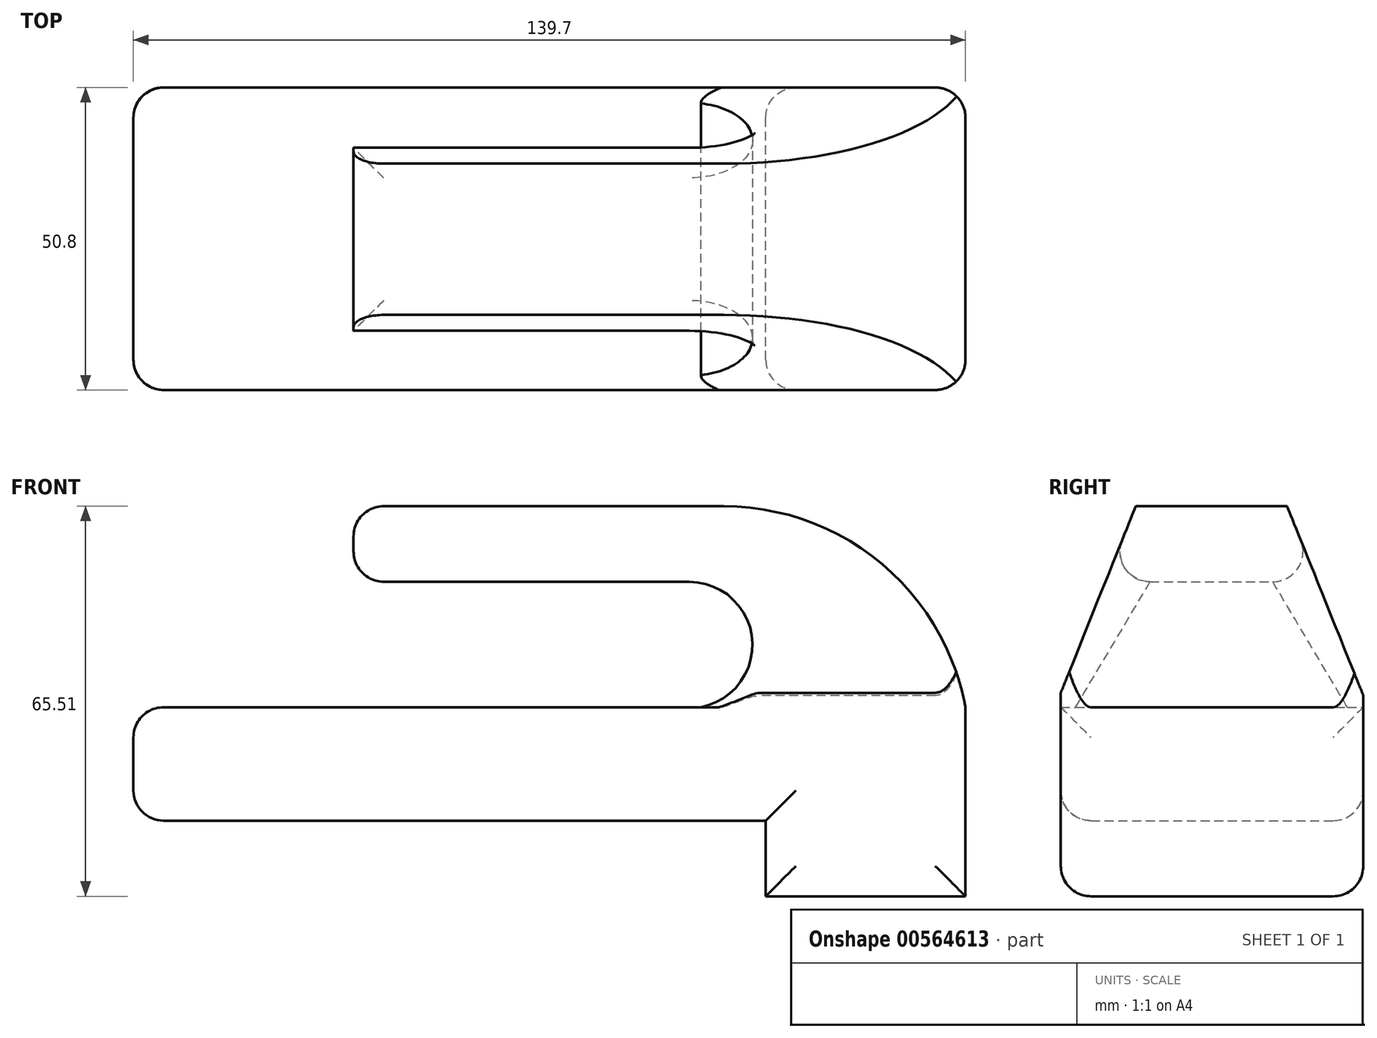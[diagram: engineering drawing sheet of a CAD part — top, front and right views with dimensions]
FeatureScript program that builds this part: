
annotation { "Feature Type Name" : "Feature", "Feature Type Description" : "" }
export const myFeature = defineFeature(function(context is Context, id is Id, definition is map)
    precondition{}
    {
        {
            var Q0;
            Q0=qCreatedBy(makeId("Front.planeOp"),FACE);
            var sketch = newSketch(context, id + "F0", { "sketchPlane" : qUnion([Q0])});
            skLineSegment(sketch, "E0.top", {"start": v(-62.26, -21) * mm, "end": v(77.44, -21) * mm});
            skLineSegment(sketch, "E0.left", {"start": v(-62.26, -1.96) * mm, "end": v(-62.26, -21) * mm});
            skLineSegment(sketch, "E0.right", {"start": v(77.44, -1.96) * mm, "end": v(77.44, -21) * mm});
            skLineSegment(sketch, "E1", {"start": v(-25.3, 31.81) * mm, "end": v(36.87, 31.81) * mm});
            skArc(sketch, "E2", {"start": v(77.44, -1.96) * mm, "mid": v(63.26, 22.26) * mm, "end": v(36.87, 31.81) * mm});
            skLineSegment(sketch, "E3", {"start": v(-25.3, 31.81) * mm, "end": v(-25.3, 19.11) * mm});
            skLineSegment(sketch, "E4", {"start": v(-25.3, 19.11) * mm, "end": v(31.09, 19.11) * mm});
            skArc(sketch, "E5", {"start": v(33.02, -1.96) * mm, "mid": v(41.67, 9.46) * mm, "end": v(31.09, 19.11) * mm});
            skLineSegment(sketch, "E6", {"start": v(-62.26, -1.96) * mm, "end": v(33.02, -1.96) * mm});
            skLineSegment(sketch, "E7.bottom", {"start": v(77.44, -21) * mm, "end": v(43.9, -21) * mm});
            skLineSegment(sketch, "E7.top", {"start": v(77.44, -33.7) * mm, "end": v(43.9, -33.7) * mm});
            skLineSegment(sketch, "E7.left", {"start": v(77.44, -21) * mm, "end": v(77.44, -33.7) * mm});
            skLineSegment(sketch, "E7.right", {"start": v(43.9, -21) * mm, "end": v(43.9, -33.7) * mm});
            skSolve(sketch);
        }
        {
            var Q0;
            Q0=qSketchRegion(id+"F0",true);
            var Q1;
            Q1 = qSketchRegion(id + "F2", true);
            extrude(context, id + "F1", {"entities" : qUnion([Q0, Q1]), "depth" : 50.8 * mm, "offsetDistance" : 25.4 * mm});
        }
        {
            var Q0;
            Q0=qCreatedBy(makeId("Right.planeOp"),FACE);
            var sketch = newSketch(context, id + "F2", { "sketchPlane" : qUnion([Q0])});
            skLineSegment(sketch, "E8", {"start": v(-12.8, 31.81) * mm, "end": v(0, 0) * mm});
            skLineSegment(sketch, "E9", {"start": v(0, 31.81) * mm, "end": v(-12.8, 31.81) * mm});
            skLineSegment(sketch, "E10", {"start": v(-38.2, 31.81) * mm, "end": v(-50.99, 0) * mm});
            skLineSegment(sketch, "E11", {"start": v(-50.99, 31.81) * mm, "end": v(-38.2, 31.81) * mm});
            skLineSegment(sketch, "E12", {"start": v(-50.99, 0) * mm, "end": v(-50.99, 31.81) * mm});
            skLineSegment(sketch, "E13", {"start": v(0, 31.81) * mm, "end": v(0, 0) * mm});
            skSolve(sketch);
        }
        {
            var Q0;
            Q0=qSketchRegion(id+"F2",true);
            extrude(context, id + "F3", {"entities" : qUnion([Q0]), "operationType" : NewBodyOperationType.REMOVE, "oppositeDirection" : true, "depth" : -152.4 * mm, "offsetDistance" : 25.4 * mm});
        }
        {
            var Q0;
            Q0=qSketchRegion(id+"F2",true);
            extrude(context, id + "F4", {"entities" : qUnion([Q0]), "operationType" : NewBodyOperationType.REMOVE, "oppositeDirection" : true, "depth" : 50.8 * mm, "offsetDistance" : 25.4 * mm});
        }
        {
            var Q0;
            {var subQ0=sQuery(id+"F2.wireOp",EDGE,"E9");var subQ1=sQuery(id+"F2.wireOp",EDGE,"E8");Q0=makeQuery(id+"F4.boolean.opBoolean","MERGE",EDGE,{"derivedFrom":[makeQuery(id+"F3.boolean.opBoolean","COPY",EDGE,{"derivedFrom":makeQuery(id+"F3.opExtrude","SWEPT_EDGE",EDGE,{"disambiguationData":[OSD([subQ1,subQ0])]})}),makeQuery(id+"F4.opExtrude","SWEPT_EDGE",EDGE,{"disambiguationData":[OSD([subQ1,subQ0])]})]});}
            var Q1;
            {var subQ0=sQuery(id+"F2.wireOp",EDGE,"E11");var subQ1=sQuery(id+"F2.wireOp",EDGE,"E10");Q1=makeQuery(id+"F4.boolean.opBoolean","MERGE",EDGE,{"derivedFrom":[makeQuery(id+"F3.boolean.opBoolean","COPY",EDGE,{"derivedFrom":makeQuery(id+"F3.opExtrude","SWEPT_EDGE",EDGE,{"disambiguationData":[OSD([subQ1,subQ0])]})}),makeQuery(id+"F4.opExtrude","SWEPT_EDGE",EDGE,{"disambiguationData":[OSD([subQ1,subQ0])]})]});}
            var Q2;
            Q2=makeQuery(id+"F4.boolean.opBoolean","INTERSECT",EDGE,{"derivedFrom":[makeQuery(id+"F1.opExtrude","SWEPT_FACE",FACE,{"disambiguationData":[OSD([sQuery(id+"F0.wireOp",EDGE,"E4")])]}),makeQuery(id+"F4.opExtrude","SWEPT_FACE",FACE,{"disambiguationData":[OSD([sQuery(id+"F2.wireOp",EDGE,"E8")])]})]});
            var Q3;
            Q3=makeQuery(id+"F1.opExtrude","SWEPT_EDGE",EDGE,{"disambiguationData":[OSD([sQuery(id+"F0.wireOp",EDGE,"E3"),sQuery(id+"F0.wireOp",EDGE,"E4")])]});
            var Q4;
            Q4=makeQuery(id+"F4.boolean.opBoolean","INTERSECT",EDGE,{"derivedFrom":[makeQuery(id+"F1.opExtrude","SWEPT_FACE",FACE,{"disambiguationData":[OSD([sQuery(id+"F0.wireOp",EDGE,"E4")])]}),makeQuery(id+"F4.opExtrude","SWEPT_FACE",FACE,{"disambiguationData":[OSD([sQuery(id+"F2.wireOp",EDGE,"E10")])]})]});
            fillet(context, id + "F5", {"entities" : qUnion([Q0, Q1, Q2, Q3, Q4]), "radius" : 5.08 * mm, "tangentPropagation" : true, "allowEdgeOverflow" : false});
        }
        {
            var Q0;
            Q0=makeQuery(id+"F1.opExtrude","SWEPT_EDGE",EDGE,{"disambiguationData":[OSD([sQuery(id+"F0.wireOp",EDGE,"E0.left"),sQuery(id+"F0.wireOp",EDGE,"E6")])]});
            var Q1;
            Q1=makeQuery(id+"F1.opExtrude","SWEPT_EDGE",EDGE,{"disambiguationData":[OSD([sQuery(id+"F0.wireOp",EDGE,"E0.top"),sQuery(id+"F0.wireOp",EDGE,"E0.left")])]});
            var Q2;
            Q2=makeQuery(id+"F1.opExtrude","CAP_EDGE",EDGE,{"disambiguationData":[OSD([sQuery(id+"F0.wireOp",EDGE,"E0.top")])],"isStart":false});
            var Q3;
            Q3=makeQuery(id+"F1.opExtrude","CAP_EDGE",EDGE,{"disambiguationData":[OSD([sQuery(id+"F0.wireOp",EDGE,"E7.right")])],"isStart":false});
            var Q4;
            Q4=makeQuery(id+"F1.opExtrude","CAP_EDGE",EDGE,{"disambiguationData":[OSD([sQuery(id+"F0.wireOp",EDGE,"E7.top")])],"isStart":false});
            var Q5;
            Q5=makeQuery(id+"F1.opExtrude","CAP_EDGE",EDGE,{"disambiguationData":[OSD([sQuery(id+"F0.wireOp",EDGE,"E0.right"),sQuery(id+"F0.wireOp",EDGE,"E7.left")])],"isStart":false});
            var Q6;
            Q6=makeQuery(id+"F1.opExtrude","CAP_EDGE",EDGE,{"disambiguationData":[OSD([sQuery(id+"F0.wireOp",EDGE,"E0.top")])],"isStart":true});
            var Q7;
            Q7=makeQuery(id+"F1.opExtrude","CAP_EDGE",EDGE,{"disambiguationData":[OSD([sQuery(id+"F0.wireOp",EDGE,"E7.right")])],"isStart":true});
            var Q8;
            Q8=makeQuery(id+"F1.opExtrude","CAP_EDGE",EDGE,{"disambiguationData":[OSD([sQuery(id+"F0.wireOp",EDGE,"E7.top")])],"isStart":true});
            var Q9;
            Q9=makeQuery(id+"F1.opExtrude","CAP_EDGE",EDGE,{"disambiguationData":[OSD([sQuery(id+"F0.wireOp",EDGE,"E0.right"),sQuery(id+"F0.wireOp",EDGE,"E7.left")])],"isStart":true});
            var Q10;
            Q10=makeQuery(id+"F1.opExtrude","CAP_EDGE",EDGE,{"disambiguationData":[OSD([sQuery(id+"F0.wireOp",EDGE,"E0.left")])],"isStart":true});
            var Q11;
            Q11=makeQuery(id+"F1.opExtrude","CAP_EDGE",EDGE,{"disambiguationData":[OSD([sQuery(id+"F0.wireOp",EDGE,"E0.left")])],"isStart":false});
            var Q12;
            Q12=makeQuery(id+"F1.opExtrude","SWEPT_EDGE",EDGE,{"disambiguationData":[OSD([sQuery(id+"F0.wireOp",EDGE,"E1"),sQuery(id+"F0.wireOp",EDGE,"E3")])]});
            fillet(context, id + "F6", {"entities" : qUnion([Q0, Q1, Q2, Q3, Q4, Q5, Q6, Q7, Q8, Q9, Q10, Q11, Q12]), "radius" : 5.08 * mm, "tangentPropagation" : true, "allowEdgeOverflow" : false});
        }
    });
